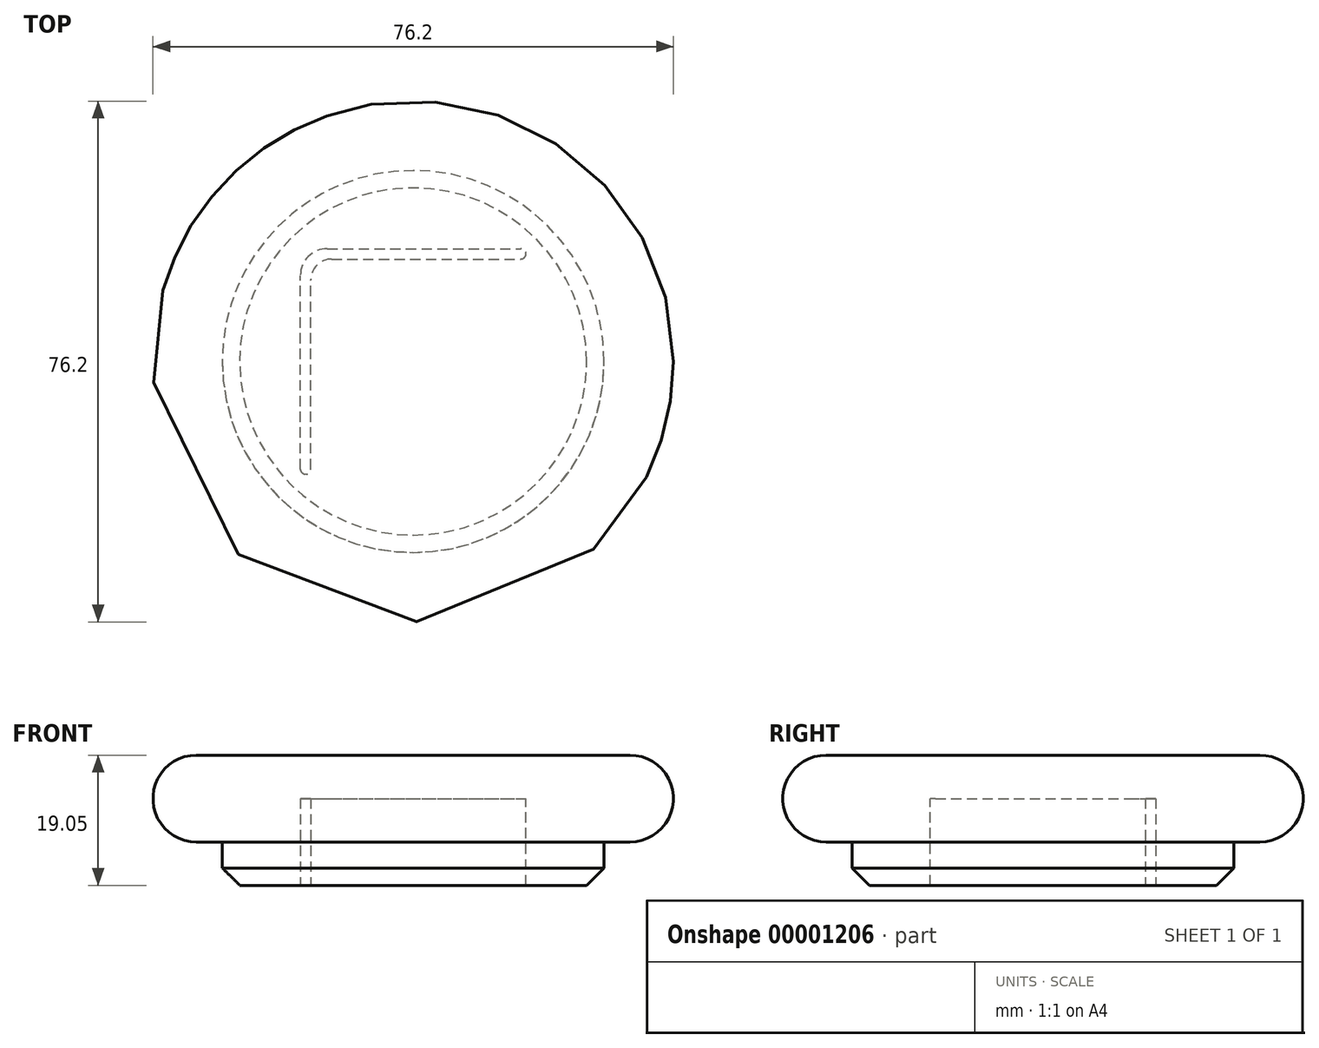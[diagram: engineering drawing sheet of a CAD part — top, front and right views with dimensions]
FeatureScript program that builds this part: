
annotation { "Feature Type Name" : "Feature", "Feature Type Description" : "" }
export const myFeature = defineFeature(function(context is Context, id is Id, definition is map)
    precondition{}
    {
        {
            var Q0;
            Q0=qCreatedBy(makeId("Front.planeOp"),FACE);
            var sketch = newSketch(context, id + "F0", { "sketchPlane" : qUnion([Q0])});
            skLineSegment(sketch, "E0", {"start": v(0, 59.72) * mm, "end": v(0, -46.33) * mm, "construction": true});
            skLineSegment(sketch, "E1", {"start": v(0, 12.7) * mm, "end": v(38.1, 12.7) * mm});
            skLineSegment(sketch, "E2", {"start": v(38.1, 12.7) * mm, "end": v(38.1, 0) * mm});
            skLineSegment(sketch, "E3", {"start": v(38.1, 0) * mm, "end": v(27.94, 0) * mm});
            skLineSegment(sketch, "E4", {"start": v(27.94, 0) * mm, "end": v(27.94, -6.35) * mm});
            skLineSegment(sketch, "E5", {"start": v(27.94, -6.35) * mm, "end": v(0, -6.35) * mm});
            skLineSegment(sketch, "E6", {"start": v(0, -6.35) * mm, "end": v(0, 12.7) * mm});
            skSolve(sketch);
        }
        {
            var Q0;
            Q0 = qSketchRegion(id + "F0", true);
            var Q1;
            Q1=sQuery(id+"F0.wireOp",EDGE,"E0");
            revolve(context, id + "F1", {"surfaceOperationType" : NewSurfaceOperationType.NEW, "entities" : qUnion([Q0]), "axis" : qUnion([Q1]), "revolveType" : RevolveType.FULL});
        }
        {
            var Q0;
            Q0=makeQuery(id+"F1.opRevolve","SWEPT_EDGE",EDGE,{"disambiguationData":[OSD([sQuery(id+"F0.wireOp",EDGE,"E1"),sQuery(id+"F0.wireOp",EDGE,"E2")])]});
            var Q1;
            Q1=makeQuery(id+"F1.opRevolve","SWEPT_EDGE",EDGE,{"disambiguationData":[OSD([sQuery(id+"F0.wireOp",EDGE,"E2"),sQuery(id+"F0.wireOp",EDGE,"E3")])]});
            fillet(context, id + "F2", {"entities" : qUnion([Q0, Q1]), "tangentPropagation" : true, "radius" : 6.35 * mm, "defaultsChanged" : true, "vertexSettings" : [], "allowEdgeOverflow" : false});
        }
        {
            var Q0;
            Q0=makeQuery(id+"F1.opRevolve","SWEPT_FACE",FACE,{"disambiguationData":[OSD([sQuery(id+"F0.wireOp",EDGE,"E5")])]});
            var sketch = newSketch(context, id + "F3", { "sketchPlane" : qUnion([Q0])});
            skLineSegment(sketch, "E7", {"start": v(-16.51, 16.51) * mm, "end": v(-16.51, -16.51) * mm});
            skLineSegment(sketch, "E8", {"start": v(-16.51, -16.51) * mm, "end": v(16.51, -16.51) * mm});
            skLineSegment(sketch, "E9", {"start": v(-14.99, 16.51) * mm, "end": v(-14.99, -14.99) * mm});
            skLineSegment(sketch, "E10", {"start": v(-14.99, -14.99) * mm, "end": v(16.51, -14.99) * mm});
            skLineSegment(sketch, "E11", {"start": v(16.51, -14.99) * mm, "end": v(16.51, -16.51) * mm});
            skLineSegment(sketch, "E12", {"start": v(-14.99, 16.51) * mm, "end": v(-16.51, 16.51) * mm});
            skSolve(sketch);
        }
        {
            var Q0;
            Q0 = qSketchRegion(id + "F3", true);
            extrude(context, id + "F4", {"entities" : qUnion([Q0]), "operationType" : NewBodyOperationType.REMOVE, "oppositeDirection" : true, "depth" : 12.7 * mm, "offsetDistance" : 25.4 * mm});
        }
        {
            var Q0;
            Q0=makeQuery(id+"F4.boolean.opBoolean","COPY",EDGE,{"derivedFrom":makeQuery(id+"F4.opExtrude","SWEPT_EDGE",EDGE,{"disambiguationData":[OSD([sQuery(id+"F3.wireOp",EDGE,"E9"),sQuery(id+"F3.wireOp",EDGE,"E10")])]})});
            fillet(context, id + "F5", {"entities" : qUnion([Q0]), "tangentPropagation" : true, "radius" : 3.05 * mm, "defaultsChanged" : true, "vertexSettings" : [], "allowEdgeOverflow" : false});
        }
        {
            var Q0;
            Q0=makeQuery(id+"F4.boolean.opBoolean","COPY",EDGE,{"derivedFrom":makeQuery(id+"F4.opExtrude","SWEPT_EDGE",EDGE,{"disambiguationData":[OSD([sQuery(id+"F3.wireOp",EDGE,"E7"),sQuery(id+"F3.wireOp",EDGE,"E8")])]})});
            fillet(context, id + "F6", {"entities" : qUnion([Q0]), "tangentPropagation" : true, "radius" : 3.94 * mm, "defaultsChanged" : true, "vertexSettings" : [], "allowEdgeOverflow" : false});
        }
        {
            var Q0;
            Q0=makeQuery(id+"F4.boolean.opBoolean","COPY",EDGE,{"derivedFrom":makeQuery(id+"F4.opExtrude","SWEPT_EDGE",EDGE,{"disambiguationData":[OSD([sQuery(id+"F3.wireOp",EDGE,"E7"),sQuery(id+"F3.wireOp",EDGE,"E12")])]})});
            var Q1;
            Q1=makeQuery(id+"F4.boolean.opBoolean","COPY",EDGE,{"derivedFrom":makeQuery(id+"F4.opExtrude","SWEPT_EDGE",EDGE,{"disambiguationData":[OSD([sQuery(id+"F3.wireOp",EDGE,"E9"),sQuery(id+"F3.wireOp",EDGE,"E12")])]})});
            var Q2;
            Q2=makeQuery(id+"F4.boolean.opBoolean","COPY",EDGE,{"derivedFrom":makeQuery(id+"F4.opExtrude","SWEPT_EDGE",EDGE,{"disambiguationData":[OSD([sQuery(id+"F3.wireOp",EDGE,"E10"),sQuery(id+"F3.wireOp",EDGE,"E11")])]})});
            var Q3;
            Q3=makeQuery(id+"F4.boolean.opBoolean","COPY",EDGE,{"derivedFrom":makeQuery(id+"F4.opExtrude","SWEPT_EDGE",EDGE,{"disambiguationData":[OSD([sQuery(id+"F3.wireOp",EDGE,"E8"),sQuery(id+"F3.wireOp",EDGE,"E11")])]})});
            fillet(context, id + "F7", {"entities" : qUnion([Q0, Q1, Q2, Q3]), "tangentPropagation" : true, "radius" : 0.76 * mm, "defaultsChanged" : true, "vertexSettings" : [], "allowEdgeOverflow" : false});
        }
        {
            var Q0;
            Q0=makeQuery(id+"F1.opRevolve","SWEPT_EDGE",EDGE,{"disambiguationData":[OSD([sQuery(id+"F0.wireOp",EDGE,"E4"),sQuery(id+"F0.wireOp",EDGE,"E5")])]});
            chamfer(context, id + "F8", {"entities" : qUnion([Q0]), "width" : 2.54 * mm, "tangentPropagation" : true});
        }
    });
